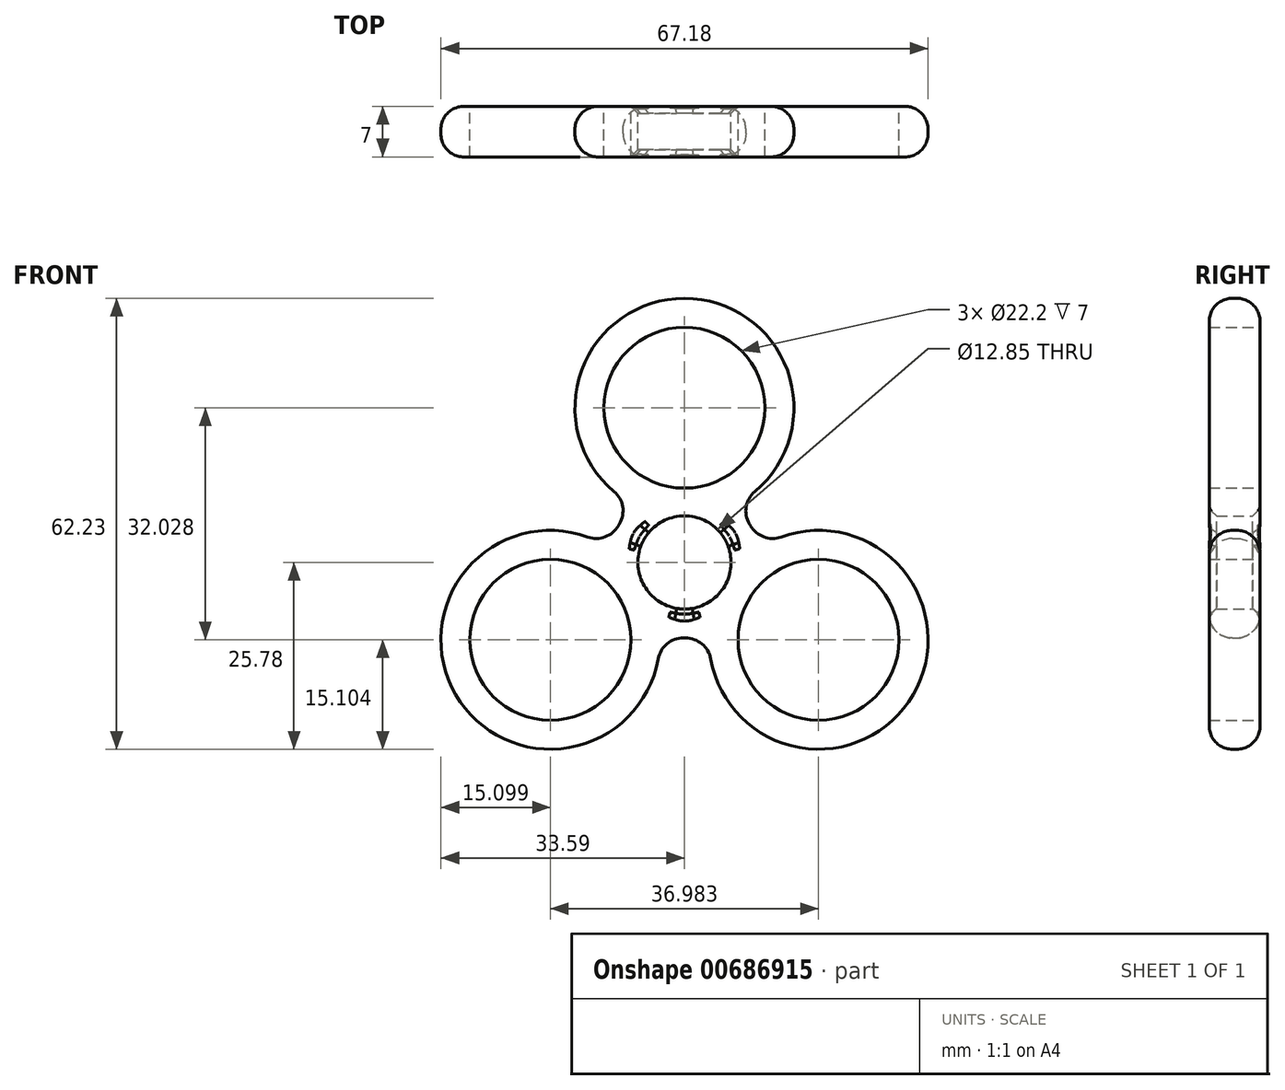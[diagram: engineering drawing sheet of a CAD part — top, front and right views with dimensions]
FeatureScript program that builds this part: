
annotation { "Feature Type Name" : "Feature", "Feature Type Description" : "" }
export const myFeature = defineFeature(function(context is Context, id is Id, definition is map)
    precondition{}
    {
        {
            var Q0;
            Q0=qCreatedBy(makeId("Front.planeOp"),FACE);
            var sketch = newSketch(context, id + "F0", { "sketchPlane" : qUnion([Q0])});
            skCircle(sketch, "E0", {"center": v(0, 0) * mm, "radius": 6.42 * mm});
            skLineSegment(sketch, "E1", {"start": v(0, 0) * mm, "end": v(0, 21.35) * mm, "construction": true});
            skLineSegment(sketch, "E2", {"start": v(0, 0) * mm, "end": v(18.5, -10.68) * mm, "construction": true});
            skLineSegment(sketch, "E3", {"start": v(0, 0) * mm, "end": v(-18.5, -10.68) * mm, "construction": true});
            skCircle(sketch, "E4", {"center": v(0, 21.35) * mm, "radius": 11.1 * mm});
            skCircle(sketch, "E5", {"center": v(18.5, -10.68) * mm, "radius": 11.1 * mm});
            skCircle(sketch, "E6", {"center": v(-18.5, -10.68) * mm, "radius": 11.1 * mm});
            skArc(sketch, "E7.0", {"start": v(9.72, 9.8) * mm, "mid": v(0, 36.45) * mm, "end": v(-9.72, 9.8) * mm});
            skArc(sketch, "E8.0", {"start": v(3.63, -13.32) * mm, "mid": v(31.57, -18.22) * mm, "end": v(13.34, 3.52) * mm});
            skArc(sketch, "E9.0", {"start": v(-13.34, 3.52) * mm, "mid": v(-31.57, -18.22) * mm, "end": v(-3.62, -13.32) * mm});
            skArc(sketch, "E10.0", {"start": v(9.1, 5.1) * mm, "mid": v(9.03, 5.21) * mm, "end": v(8.96, 5.33) * mm});
            skArc(sketch, "E11.trimOffspring", {"start": v(-0.12, -10.44) * mm, "mid": v(0, -10.44) * mm, "end": v(0.14, -10.44) * mm});
            skArc(sketch, "E12.trimOffspring", {"start": v(-8.96, 5.33) * mm, "mid": v(-9.03, 5.21) * mm, "end": v(-9.1, 5.1) * mm});
            skPoint(sketch, "E13.visualSharp", {"position": v(6.82, 7.88) * mm});
            skArc(sketch, "E13.filletArc", {"start": v(9.72, 9.8) * mm, "mid": v(8.52, 7.7) * mm, "end": v(8.96, 5.33) * mm});
            skPoint(sketch, "E14.visualSharp", {"position": v(10.24, 1.97) * mm});
            skArc(sketch, "E14.filletArc", {"start": v(9.1, 5.1) * mm, "mid": v(10.93, 3.53) * mm, "end": v(13.34, 3.52) * mm});
            skPoint(sketch, "E15.visualSharp", {"position": v(-6.82, 7.88) * mm});
            skArc(sketch, "E15.filletArc", {"start": v(-8.96, 5.33) * mm, "mid": v(-8.52, 7.7) * mm, "end": v(-9.72, 9.8) * mm});
            skPoint(sketch, "E16.visualSharp", {"position": v(-10.24, 1.97) * mm});
            skArc(sketch, "E16.filletArc", {"start": v(-13.34, 3.52) * mm, "mid": v(-10.93, 3.53) * mm, "end": v(-9.1, 5.1) * mm});
            skPoint(sketch, "E17.visualSharp", {"position": v(-3.41, -9.85) * mm});
            skArc(sketch, "E17.filletArc", {"start": v(-0.12, -10.44) * mm, "mid": v(-2.4, -11.23) * mm, "end": v(-3.62, -13.32) * mm});
            skPoint(sketch, "E18.visualSharp", {"position": v(3.41, -9.88) * mm});
            skArc(sketch, "E18.filletArc", {"start": v(3.63, -13.32) * mm, "mid": v(2.41, -11.24) * mm, "end": v(0.14, -10.44) * mm});
            skSolve(sketch);
        }
        {
            var Q0;
            Q0 = qSketchRegion(id + "F0", true);
            extrude(context, id + "F1", {"entities" : qUnion([Q0]), "endBound" : BoundingType.SYMMETRIC, "depth" : 7 * mm, "offsetDistance" : 25 * mm});
        }
        {
            var Q0;
            Q0=makeQuery(id+"F1.opExtrude","CAP_EDGE",EDGE,{"disambiguationData":[OSD([sQuery(id+"F0.wireOp",EDGE,"E15.filletArc")])],"isStart":false});
            var Q1;
            Q1=makeQuery(id+"F1.opExtrude","CAP_EDGE",EDGE,{"disambiguationData":[OSD([sQuery(id+"F0.wireOp",EDGE,"E15.filletArc")])],"isStart":true});
            fillet(context, id + "F2", {"entities" : qUnion([Q0, Q1]), "radius" : 3.2 * mm, "tangentPropagation" : true, "allowEdgeOverflow" : false});
        }
        {
            var Q0;
            Q0=makeQuery(id+"F1.opExtrude","CAP_EDGE",EDGE,{"disambiguationData":[OSD([sQuery(id+"F0.wireOp",EDGE,"E0")])],"isStart":false});
            var Q1;
            Q1=makeQuery(id+"F1.opExtrude","CAP_EDGE",EDGE,{"disambiguationData":[OSD([sQuery(id+"F0.wireOp",EDGE,"E0")])],"isStart":true});
            chamfer(context, id + "F3", {"entities" : qUnion([Q0, Q1]), "width" : 1 * mm, "tangentPropagation" : true});
        }
        {
            var Q0;
            {var subQ0=sQuery(id+"F0.wireOp",EDGE,"E15.filletArc");Q0=makeQuery(id+"F3.opChamfer","BLEND_EDGE",EDGE,{"blendedFrom":[makeQuery(id+"F1.opExtrude","CAP_EDGE",EDGE,{"disambiguationData":[OSD([sQuery(id+"F0.wireOp",EDGE,"E0")])],"isStart":true}),makeQuery(id+"F2.opFillet","BLEND_FACE",FACE,{"disambiguationData":[OSD([subQ0]),TDD([makeQuery(id+"F1.opExtrude","CAP_EDGE",EDGE,{"disambiguationData":[OSD([subQ0])],"isStart":true})])]})],"blendedInto":[makeQuery(id+"F2.opFillet","BLEND_FACE",FACE,{"disambiguationData":[OSD([subQ0]),TDD([makeQuery(id+"F1.opExtrude","CAP_EDGE",EDGE,{"disambiguationData":[OSD([subQ0])],"isStart":true})])]})]});}
            var Q1;
            {var subQ0=sQuery(id+"F0.wireOp",EDGE,"E16.filletArc");Q1=makeQuery(id+"F3.opChamfer","BLEND_EDGE",EDGE,{"blendedFrom":[makeQuery(id+"F1.opExtrude","CAP_EDGE",EDGE,{"disambiguationData":[OSD([sQuery(id+"F0.wireOp",EDGE,"E0")])],"isStart":true}),makeQuery(id+"F2.opFillet","BLEND_FACE",FACE,{"disambiguationData":[OSD([subQ0]),TDD([makeQuery(id+"F1.opExtrude","CAP_EDGE",EDGE,{"disambiguationData":[OSD([subQ0])],"isStart":true})])]})],"blendedInto":[makeQuery(id+"F2.opFillet","BLEND_FACE",FACE,{"disambiguationData":[OSD([subQ0]),TDD([makeQuery(id+"F1.opExtrude","CAP_EDGE",EDGE,{"disambiguationData":[OSD([subQ0])],"isStart":true})])]})]});}
            var Q2;
            {var subQ0=sQuery(id+"F0.wireOp",EDGE,"E12.trimOffspring");Q2=makeQuery(id+"F3.opChamfer","BLEND_EDGE",EDGE,{"blendedFrom":[makeQuery(id+"F1.opExtrude","CAP_EDGE",EDGE,{"disambiguationData":[OSD([sQuery(id+"F0.wireOp",EDGE,"E0")])],"isStart":true}),makeQuery(id+"F2.opFillet","BLEND_FACE",FACE,{"disambiguationData":[OSD([subQ0]),TDD([makeQuery(id+"F1.opExtrude","CAP_EDGE",EDGE,{"disambiguationData":[OSD([subQ0])],"isStart":true})])]})],"blendedInto":[makeQuery(id+"F2.opFillet","BLEND_FACE",FACE,{"disambiguationData":[OSD([subQ0]),TDD([makeQuery(id+"F1.opExtrude","CAP_EDGE",EDGE,{"disambiguationData":[OSD([subQ0])],"isStart":true})])]})]});}
            var Q3;
            {var subQ0=sQuery(id+"F0.wireOp",EDGE,"E0");Q3=makeQuery(id+"F3.opChamfer","BLEND_EDGE",EDGE,{"disambiguationData":[OD(2.0)],"blendedFrom":[makeQuery(id+"F1.opExtrude","CAP_EDGE",EDGE,{"disambiguationData":[OSD([subQ0])],"isStart":true}),makeQuery(id+"F1.opExtrude","CAP_FACE",FACE,{"disambiguationData":[OSD([subQ0,sQuery(id+"F0.wireOp",EDGE,"E4"),sQuery(id+"F0.wireOp",EDGE,"E5"),sQuery(id+"F0.wireOp",EDGE,"E6"),sQuery(id+"F0.wireOp",EDGE,"E7.0"),sQuery(id+"F0.wireOp",EDGE,"E8.0"),sQuery(id+"F0.wireOp",EDGE,"E9.0"),sQuery(id+"F0.wireOp",EDGE,"E10.0"),sQuery(id+"F0.wireOp",EDGE,"E11.trimOffspring"),sQuery(id+"F0.wireOp",EDGE,"E12.trimOffspring"),sQuery(id+"F0.wireOp",EDGE,"E13.filletArc"),sQuery(id+"F0.wireOp",EDGE,"E14.filletArc"),sQuery(id+"F0.wireOp",EDGE,"E15.filletArc"),sQuery(id+"F0.wireOp",EDGE,"E16.filletArc"),sQuery(id+"F0.wireOp",EDGE,"E17.filletArc"),sQuery(id+"F0.wireOp",EDGE,"E18.filletArc")])],"isStart":true})],"blendedInto":[makeQuery(id+"F1.opExtrude","CAP_FACE",FACE,{"disambiguationData":[OSD([subQ0,sQuery(id+"F0.wireOp",EDGE,"E4"),sQuery(id+"F0.wireOp",EDGE,"E5"),sQuery(id+"F0.wireOp",EDGE,"E6"),sQuery(id+"F0.wireOp",EDGE,"E7.0"),sQuery(id+"F0.wireOp",EDGE,"E8.0"),sQuery(id+"F0.wireOp",EDGE,"E9.0"),sQuery(id+"F0.wireOp",EDGE,"E10.0"),sQuery(id+"F0.wireOp",EDGE,"E11.trimOffspring"),sQuery(id+"F0.wireOp",EDGE,"E12.trimOffspring"),sQuery(id+"F0.wireOp",EDGE,"E13.filletArc"),sQuery(id+"F0.wireOp",EDGE,"E14.filletArc"),sQuery(id+"F0.wireOp",EDGE,"E15.filletArc"),sQuery(id+"F0.wireOp",EDGE,"E16.filletArc"),sQuery(id+"F0.wireOp",EDGE,"E17.filletArc"),sQuery(id+"F0.wireOp",EDGE,"E18.filletArc")])],"isStart":true})]});}
            var Q4;
            {var subQ0=sQuery(id+"F0.wireOp",EDGE,"E0");Q4=makeQuery(id+"F3.opChamfer","BLEND_EDGE",EDGE,{"disambiguationData":[OD(0.0)],"blendedFrom":[makeQuery(id+"F1.opExtrude","CAP_EDGE",EDGE,{"disambiguationData":[OSD([subQ0])],"isStart":true}),makeQuery(id+"F1.opExtrude","CAP_FACE",FACE,{"disambiguationData":[OSD([subQ0,sQuery(id+"F0.wireOp",EDGE,"E4"),sQuery(id+"F0.wireOp",EDGE,"E5"),sQuery(id+"F0.wireOp",EDGE,"E6"),sQuery(id+"F0.wireOp",EDGE,"E7.0"),sQuery(id+"F0.wireOp",EDGE,"E8.0"),sQuery(id+"F0.wireOp",EDGE,"E9.0"),sQuery(id+"F0.wireOp",EDGE,"E10.0"),sQuery(id+"F0.wireOp",EDGE,"E11.trimOffspring"),sQuery(id+"F0.wireOp",EDGE,"E12.trimOffspring"),sQuery(id+"F0.wireOp",EDGE,"E13.filletArc"),sQuery(id+"F0.wireOp",EDGE,"E14.filletArc"),sQuery(id+"F0.wireOp",EDGE,"E15.filletArc"),sQuery(id+"F0.wireOp",EDGE,"E16.filletArc"),sQuery(id+"F0.wireOp",EDGE,"E17.filletArc"),sQuery(id+"F0.wireOp",EDGE,"E18.filletArc")])],"isStart":true})],"blendedInto":[makeQuery(id+"F1.opExtrude","CAP_FACE",FACE,{"disambiguationData":[OSD([subQ0,sQuery(id+"F0.wireOp",EDGE,"E4"),sQuery(id+"F0.wireOp",EDGE,"E5"),sQuery(id+"F0.wireOp",EDGE,"E6"),sQuery(id+"F0.wireOp",EDGE,"E7.0"),sQuery(id+"F0.wireOp",EDGE,"E8.0"),sQuery(id+"F0.wireOp",EDGE,"E9.0"),sQuery(id+"F0.wireOp",EDGE,"E10.0"),sQuery(id+"F0.wireOp",EDGE,"E11.trimOffspring"),sQuery(id+"F0.wireOp",EDGE,"E12.trimOffspring"),sQuery(id+"F0.wireOp",EDGE,"E13.filletArc"),sQuery(id+"F0.wireOp",EDGE,"E14.filletArc"),sQuery(id+"F0.wireOp",EDGE,"E15.filletArc"),sQuery(id+"F0.wireOp",EDGE,"E16.filletArc"),sQuery(id+"F0.wireOp",EDGE,"E17.filletArc"),sQuery(id+"F0.wireOp",EDGE,"E18.filletArc")])],"isStart":true})]});}
            var Q5;
            {var subQ0=sQuery(id+"F0.wireOp",EDGE,"E13.filletArc");Q5=makeQuery(id+"F3.opChamfer","BLEND_EDGE",EDGE,{"blendedFrom":[makeQuery(id+"F1.opExtrude","CAP_EDGE",EDGE,{"disambiguationData":[OSD([sQuery(id+"F0.wireOp",EDGE,"E0")])],"isStart":true}),makeQuery(id+"F2.opFillet","BLEND_FACE",FACE,{"disambiguationData":[OSD([subQ0]),TDD([makeQuery(id+"F1.opExtrude","CAP_EDGE",EDGE,{"disambiguationData":[OSD([subQ0])],"isStart":true})])]})],"blendedInto":[makeQuery(id+"F2.opFillet","BLEND_FACE",FACE,{"disambiguationData":[OSD([subQ0]),TDD([makeQuery(id+"F1.opExtrude","CAP_EDGE",EDGE,{"disambiguationData":[OSD([subQ0])],"isStart":true})])]})]});}
            var Q6;
            {var subQ0=sQuery(id+"F0.wireOp",EDGE,"E14.filletArc");Q6=makeQuery(id+"F3.opChamfer","BLEND_EDGE",EDGE,{"blendedFrom":[makeQuery(id+"F1.opExtrude","CAP_EDGE",EDGE,{"disambiguationData":[OSD([sQuery(id+"F0.wireOp",EDGE,"E0")])],"isStart":true}),makeQuery(id+"F2.opFillet","BLEND_FACE",FACE,{"disambiguationData":[OSD([subQ0]),TDD([makeQuery(id+"F1.opExtrude","CAP_EDGE",EDGE,{"disambiguationData":[OSD([subQ0])],"isStart":true})])]})],"blendedInto":[makeQuery(id+"F2.opFillet","BLEND_FACE",FACE,{"disambiguationData":[OSD([subQ0]),TDD([makeQuery(id+"F1.opExtrude","CAP_EDGE",EDGE,{"disambiguationData":[OSD([subQ0])],"isStart":true})])]})]});}
            var Q7;
            {var subQ0=sQuery(id+"F0.wireOp",EDGE,"E10.0");Q7=makeQuery(id+"F3.opChamfer","BLEND_EDGE",EDGE,{"blendedFrom":[makeQuery(id+"F1.opExtrude","CAP_EDGE",EDGE,{"disambiguationData":[OSD([sQuery(id+"F0.wireOp",EDGE,"E0")])],"isStart":true}),makeQuery(id+"F2.opFillet","BLEND_FACE",FACE,{"disambiguationData":[OSD([subQ0]),TDD([makeQuery(id+"F1.opExtrude","CAP_EDGE",EDGE,{"disambiguationData":[OSD([subQ0])],"isStart":true})])]})],"blendedInto":[makeQuery(id+"F2.opFillet","BLEND_FACE",FACE,{"disambiguationData":[OSD([subQ0]),TDD([makeQuery(id+"F1.opExtrude","CAP_EDGE",EDGE,{"disambiguationData":[OSD([subQ0])],"isStart":true})])]})]});}
            var Q8;
            {var subQ0=sQuery(id+"F0.wireOp",EDGE,"E0");Q8=makeQuery(id+"F3.opChamfer","BLEND_EDGE",EDGE,{"disambiguationData":[OD(1.0)],"blendedFrom":[makeQuery(id+"F1.opExtrude","CAP_EDGE",EDGE,{"disambiguationData":[OSD([subQ0])],"isStart":true}),makeQuery(id+"F1.opExtrude","CAP_FACE",FACE,{"disambiguationData":[OSD([subQ0,sQuery(id+"F0.wireOp",EDGE,"E4"),sQuery(id+"F0.wireOp",EDGE,"E5"),sQuery(id+"F0.wireOp",EDGE,"E6"),sQuery(id+"F0.wireOp",EDGE,"E7.0"),sQuery(id+"F0.wireOp",EDGE,"E8.0"),sQuery(id+"F0.wireOp",EDGE,"E9.0"),sQuery(id+"F0.wireOp",EDGE,"E10.0"),sQuery(id+"F0.wireOp",EDGE,"E11.trimOffspring"),sQuery(id+"F0.wireOp",EDGE,"E12.trimOffspring"),sQuery(id+"F0.wireOp",EDGE,"E13.filletArc"),sQuery(id+"F0.wireOp",EDGE,"E14.filletArc"),sQuery(id+"F0.wireOp",EDGE,"E15.filletArc"),sQuery(id+"F0.wireOp",EDGE,"E16.filletArc"),sQuery(id+"F0.wireOp",EDGE,"E17.filletArc"),sQuery(id+"F0.wireOp",EDGE,"E18.filletArc")])],"isStart":true})],"blendedInto":[makeQuery(id+"F1.opExtrude","CAP_FACE",FACE,{"disambiguationData":[OSD([subQ0,sQuery(id+"F0.wireOp",EDGE,"E4"),sQuery(id+"F0.wireOp",EDGE,"E5"),sQuery(id+"F0.wireOp",EDGE,"E6"),sQuery(id+"F0.wireOp",EDGE,"E7.0"),sQuery(id+"F0.wireOp",EDGE,"E8.0"),sQuery(id+"F0.wireOp",EDGE,"E9.0"),sQuery(id+"F0.wireOp",EDGE,"E10.0"),sQuery(id+"F0.wireOp",EDGE,"E11.trimOffspring"),sQuery(id+"F0.wireOp",EDGE,"E12.trimOffspring"),sQuery(id+"F0.wireOp",EDGE,"E13.filletArc"),sQuery(id+"F0.wireOp",EDGE,"E14.filletArc"),sQuery(id+"F0.wireOp",EDGE,"E15.filletArc"),sQuery(id+"F0.wireOp",EDGE,"E16.filletArc"),sQuery(id+"F0.wireOp",EDGE,"E17.filletArc"),sQuery(id+"F0.wireOp",EDGE,"E18.filletArc")])],"isStart":true})]});}
            var Q9;
            {var subQ0=sQuery(id+"F0.wireOp",EDGE,"E18.filletArc");Q9=makeQuery(id+"F3.opChamfer","BLEND_EDGE",EDGE,{"blendedFrom":[makeQuery(id+"F1.opExtrude","CAP_EDGE",EDGE,{"disambiguationData":[OSD([sQuery(id+"F0.wireOp",EDGE,"E0")])],"isStart":true}),makeQuery(id+"F2.opFillet","BLEND_FACE",FACE,{"disambiguationData":[OSD([subQ0]),TDD([makeQuery(id+"F1.opExtrude","CAP_EDGE",EDGE,{"disambiguationData":[OSD([subQ0])],"isStart":true})])]})],"blendedInto":[makeQuery(id+"F2.opFillet","BLEND_FACE",FACE,{"disambiguationData":[OSD([subQ0]),TDD([makeQuery(id+"F1.opExtrude","CAP_EDGE",EDGE,{"disambiguationData":[OSD([subQ0])],"isStart":true})])]})]});}
            var Q10;
            {var subQ0=sQuery(id+"F0.wireOp",EDGE,"E17.filletArc");Q10=makeQuery(id+"F3.opChamfer","BLEND_EDGE",EDGE,{"blendedFrom":[makeQuery(id+"F1.opExtrude","CAP_EDGE",EDGE,{"disambiguationData":[OSD([sQuery(id+"F0.wireOp",EDGE,"E0")])],"isStart":true}),makeQuery(id+"F2.opFillet","BLEND_FACE",FACE,{"disambiguationData":[OSD([subQ0]),TDD([makeQuery(id+"F1.opExtrude","CAP_EDGE",EDGE,{"disambiguationData":[OSD([subQ0])],"isStart":true})])]})],"blendedInto":[makeQuery(id+"F2.opFillet","BLEND_FACE",FACE,{"disambiguationData":[OSD([subQ0]),TDD([makeQuery(id+"F1.opExtrude","CAP_EDGE",EDGE,{"disambiguationData":[OSD([subQ0])],"isStart":true})])]})]});}
            var Q11;
            {var subQ0=sQuery(id+"F0.wireOp",EDGE,"E11.trimOffspring");Q11=makeQuery(id+"F3.opChamfer","BLEND_EDGE",EDGE,{"blendedFrom":[makeQuery(id+"F1.opExtrude","CAP_EDGE",EDGE,{"disambiguationData":[OSD([sQuery(id+"F0.wireOp",EDGE,"E0")])],"isStart":true}),makeQuery(id+"F2.opFillet","BLEND_FACE",FACE,{"disambiguationData":[OSD([subQ0]),TDD([makeQuery(id+"F1.opExtrude","CAP_EDGE",EDGE,{"disambiguationData":[OSD([subQ0])],"isStart":true})])]})],"blendedInto":[makeQuery(id+"F2.opFillet","BLEND_FACE",FACE,{"disambiguationData":[OSD([subQ0]),TDD([makeQuery(id+"F1.opExtrude","CAP_EDGE",EDGE,{"disambiguationData":[OSD([subQ0])],"isStart":true})])]})]});}
            var Q12;
            {var subQ0=sQuery(id+"F0.wireOp",EDGE,"E0");Q12=makeQuery(id+"F3.opChamfer","BLEND_EDGE",EDGE,{"disambiguationData":[OD(1.0)],"blendedFrom":[makeQuery(id+"F1.opExtrude","CAP_EDGE",EDGE,{"disambiguationData":[OSD([subQ0])],"isStart":false}),makeQuery(id+"F1.opExtrude","CAP_FACE",FACE,{"disambiguationData":[OSD([subQ0,sQuery(id+"F0.wireOp",EDGE,"E4"),sQuery(id+"F0.wireOp",EDGE,"E5"),sQuery(id+"F0.wireOp",EDGE,"E6"),sQuery(id+"F0.wireOp",EDGE,"E7.0"),sQuery(id+"F0.wireOp",EDGE,"E8.0"),sQuery(id+"F0.wireOp",EDGE,"E9.0"),sQuery(id+"F0.wireOp",EDGE,"E10.0"),sQuery(id+"F0.wireOp",EDGE,"E11.trimOffspring"),sQuery(id+"F0.wireOp",EDGE,"E12.trimOffspring"),sQuery(id+"F0.wireOp",EDGE,"E13.filletArc"),sQuery(id+"F0.wireOp",EDGE,"E14.filletArc"),sQuery(id+"F0.wireOp",EDGE,"E15.filletArc"),sQuery(id+"F0.wireOp",EDGE,"E16.filletArc"),sQuery(id+"F0.wireOp",EDGE,"E17.filletArc"),sQuery(id+"F0.wireOp",EDGE,"E18.filletArc")])],"isStart":false})],"blendedInto":[makeQuery(id+"F1.opExtrude","CAP_FACE",FACE,{"disambiguationData":[OSD([subQ0,sQuery(id+"F0.wireOp",EDGE,"E4"),sQuery(id+"F0.wireOp",EDGE,"E5"),sQuery(id+"F0.wireOp",EDGE,"E6"),sQuery(id+"F0.wireOp",EDGE,"E7.0"),sQuery(id+"F0.wireOp",EDGE,"E8.0"),sQuery(id+"F0.wireOp",EDGE,"E9.0"),sQuery(id+"F0.wireOp",EDGE,"E10.0"),sQuery(id+"F0.wireOp",EDGE,"E11.trimOffspring"),sQuery(id+"F0.wireOp",EDGE,"E12.trimOffspring"),sQuery(id+"F0.wireOp",EDGE,"E13.filletArc"),sQuery(id+"F0.wireOp",EDGE,"E14.filletArc"),sQuery(id+"F0.wireOp",EDGE,"E15.filletArc"),sQuery(id+"F0.wireOp",EDGE,"E16.filletArc"),sQuery(id+"F0.wireOp",EDGE,"E17.filletArc"),sQuery(id+"F0.wireOp",EDGE,"E18.filletArc")])],"isStart":false})]});}
            var Q13;
            {var subQ0=sQuery(id+"F0.wireOp",EDGE,"E14.filletArc");Q13=makeQuery(id+"F3.opChamfer","BLEND_EDGE",EDGE,{"blendedFrom":[makeQuery(id+"F1.opExtrude","CAP_EDGE",EDGE,{"disambiguationData":[OSD([sQuery(id+"F0.wireOp",EDGE,"E0")])],"isStart":false}),makeQuery(id+"F2.opFillet","BLEND_FACE",FACE,{"disambiguationData":[OSD([subQ0]),TDD([makeQuery(id+"F1.opExtrude","CAP_EDGE",EDGE,{"disambiguationData":[OSD([subQ0])],"isStart":false})])]})],"blendedInto":[makeQuery(id+"F2.opFillet","BLEND_FACE",FACE,{"disambiguationData":[OSD([subQ0]),TDD([makeQuery(id+"F1.opExtrude","CAP_EDGE",EDGE,{"disambiguationData":[OSD([subQ0])],"isStart":false})])]})]});}
            var Q14;
            {var subQ0=sQuery(id+"F0.wireOp",EDGE,"E10.0");Q14=makeQuery(id+"F3.opChamfer","BLEND_EDGE",EDGE,{"blendedFrom":[makeQuery(id+"F1.opExtrude","CAP_EDGE",EDGE,{"disambiguationData":[OSD([sQuery(id+"F0.wireOp",EDGE,"E0")])],"isStart":false}),makeQuery(id+"F2.opFillet","BLEND_FACE",FACE,{"disambiguationData":[OSD([subQ0]),TDD([makeQuery(id+"F1.opExtrude","CAP_EDGE",EDGE,{"disambiguationData":[OSD([subQ0])],"isStart":false})])]})],"blendedInto":[makeQuery(id+"F2.opFillet","BLEND_FACE",FACE,{"disambiguationData":[OSD([subQ0]),TDD([makeQuery(id+"F1.opExtrude","CAP_EDGE",EDGE,{"disambiguationData":[OSD([subQ0])],"isStart":false})])]})]});}
            var Q15;
            {var subQ0=sQuery(id+"F0.wireOp",EDGE,"E13.filletArc");Q15=makeQuery(id+"F3.opChamfer","BLEND_EDGE",EDGE,{"blendedFrom":[makeQuery(id+"F1.opExtrude","CAP_EDGE",EDGE,{"disambiguationData":[OSD([sQuery(id+"F0.wireOp",EDGE,"E0")])],"isStart":false}),makeQuery(id+"F2.opFillet","BLEND_FACE",FACE,{"disambiguationData":[OSD([subQ0]),TDD([makeQuery(id+"F1.opExtrude","CAP_EDGE",EDGE,{"disambiguationData":[OSD([subQ0])],"isStart":false})])]})],"blendedInto":[makeQuery(id+"F2.opFillet","BLEND_FACE",FACE,{"disambiguationData":[OSD([subQ0]),TDD([makeQuery(id+"F1.opExtrude","CAP_EDGE",EDGE,{"disambiguationData":[OSD([subQ0])],"isStart":false})])]})]});}
            var Q16;
            {var subQ0=sQuery(id+"F0.wireOp",EDGE,"E0");Q16=makeQuery(id+"F3.opChamfer","BLEND_EDGE",EDGE,{"disambiguationData":[OD(0.0)],"blendedFrom":[makeQuery(id+"F1.opExtrude","CAP_EDGE",EDGE,{"disambiguationData":[OSD([subQ0])],"isStart":false}),makeQuery(id+"F1.opExtrude","CAP_FACE",FACE,{"disambiguationData":[OSD([subQ0,sQuery(id+"F0.wireOp",EDGE,"E4"),sQuery(id+"F0.wireOp",EDGE,"E5"),sQuery(id+"F0.wireOp",EDGE,"E6"),sQuery(id+"F0.wireOp",EDGE,"E7.0"),sQuery(id+"F0.wireOp",EDGE,"E8.0"),sQuery(id+"F0.wireOp",EDGE,"E9.0"),sQuery(id+"F0.wireOp",EDGE,"E10.0"),sQuery(id+"F0.wireOp",EDGE,"E11.trimOffspring"),sQuery(id+"F0.wireOp",EDGE,"E12.trimOffspring"),sQuery(id+"F0.wireOp",EDGE,"E13.filletArc"),sQuery(id+"F0.wireOp",EDGE,"E14.filletArc"),sQuery(id+"F0.wireOp",EDGE,"E15.filletArc"),sQuery(id+"F0.wireOp",EDGE,"E16.filletArc"),sQuery(id+"F0.wireOp",EDGE,"E17.filletArc"),sQuery(id+"F0.wireOp",EDGE,"E18.filletArc")])],"isStart":false})],"blendedInto":[makeQuery(id+"F1.opExtrude","CAP_FACE",FACE,{"disambiguationData":[OSD([subQ0,sQuery(id+"F0.wireOp",EDGE,"E4"),sQuery(id+"F0.wireOp",EDGE,"E5"),sQuery(id+"F0.wireOp",EDGE,"E6"),sQuery(id+"F0.wireOp",EDGE,"E7.0"),sQuery(id+"F0.wireOp",EDGE,"E8.0"),sQuery(id+"F0.wireOp",EDGE,"E9.0"),sQuery(id+"F0.wireOp",EDGE,"E10.0"),sQuery(id+"F0.wireOp",EDGE,"E11.trimOffspring"),sQuery(id+"F0.wireOp",EDGE,"E12.trimOffspring"),sQuery(id+"F0.wireOp",EDGE,"E13.filletArc"),sQuery(id+"F0.wireOp",EDGE,"E14.filletArc"),sQuery(id+"F0.wireOp",EDGE,"E15.filletArc"),sQuery(id+"F0.wireOp",EDGE,"E16.filletArc"),sQuery(id+"F0.wireOp",EDGE,"E17.filletArc"),sQuery(id+"F0.wireOp",EDGE,"E18.filletArc")])],"isStart":false})]});}
            var Q17;
            {var subQ0=sQuery(id+"F0.wireOp",EDGE,"E15.filletArc");Q17=makeQuery(id+"F3.opChamfer","BLEND_EDGE",EDGE,{"blendedFrom":[makeQuery(id+"F1.opExtrude","CAP_EDGE",EDGE,{"disambiguationData":[OSD([sQuery(id+"F0.wireOp",EDGE,"E0")])],"isStart":false}),makeQuery(id+"F2.opFillet","BLEND_FACE",FACE,{"disambiguationData":[OSD([subQ0]),TDD([makeQuery(id+"F1.opExtrude","CAP_EDGE",EDGE,{"disambiguationData":[OSD([subQ0])],"isStart":false})])]})],"blendedInto":[makeQuery(id+"F2.opFillet","BLEND_FACE",FACE,{"disambiguationData":[OSD([subQ0]),TDD([makeQuery(id+"F1.opExtrude","CAP_EDGE",EDGE,{"disambiguationData":[OSD([subQ0])],"isStart":false})])]})]});}
            var Q18;
            {var subQ0=sQuery(id+"F0.wireOp",EDGE,"E12.trimOffspring");Q18=makeQuery(id+"F3.opChamfer","BLEND_EDGE",EDGE,{"blendedFrom":[makeQuery(id+"F1.opExtrude","CAP_EDGE",EDGE,{"disambiguationData":[OSD([sQuery(id+"F0.wireOp",EDGE,"E0")])],"isStart":false}),makeQuery(id+"F2.opFillet","BLEND_FACE",FACE,{"disambiguationData":[OSD([subQ0]),TDD([makeQuery(id+"F1.opExtrude","CAP_EDGE",EDGE,{"disambiguationData":[OSD([subQ0])],"isStart":false})])]})],"blendedInto":[makeQuery(id+"F2.opFillet","BLEND_FACE",FACE,{"disambiguationData":[OSD([subQ0]),TDD([makeQuery(id+"F1.opExtrude","CAP_EDGE",EDGE,{"disambiguationData":[OSD([subQ0])],"isStart":false})])]})]});}
            var Q19;
            {var subQ0=sQuery(id+"F0.wireOp",EDGE,"E16.filletArc");Q19=makeQuery(id+"F3.opChamfer","BLEND_EDGE",EDGE,{"blendedFrom":[makeQuery(id+"F1.opExtrude","CAP_EDGE",EDGE,{"disambiguationData":[OSD([sQuery(id+"F0.wireOp",EDGE,"E0")])],"isStart":false}),makeQuery(id+"F2.opFillet","BLEND_FACE",FACE,{"disambiguationData":[OSD([subQ0]),TDD([makeQuery(id+"F1.opExtrude","CAP_EDGE",EDGE,{"disambiguationData":[OSD([subQ0])],"isStart":false})])]})],"blendedInto":[makeQuery(id+"F2.opFillet","BLEND_FACE",FACE,{"disambiguationData":[OSD([subQ0]),TDD([makeQuery(id+"F1.opExtrude","CAP_EDGE",EDGE,{"disambiguationData":[OSD([subQ0])],"isStart":false})])]})]});}
            var Q20;
            {var subQ0=sQuery(id+"F0.wireOp",EDGE,"E0");Q20=makeQuery(id+"F3.opChamfer","BLEND_EDGE",EDGE,{"disambiguationData":[OD(2.0)],"blendedFrom":[makeQuery(id+"F1.opExtrude","CAP_EDGE",EDGE,{"disambiguationData":[OSD([subQ0])],"isStart":false}),makeQuery(id+"F1.opExtrude","CAP_FACE",FACE,{"disambiguationData":[OSD([subQ0,sQuery(id+"F0.wireOp",EDGE,"E4"),sQuery(id+"F0.wireOp",EDGE,"E5"),sQuery(id+"F0.wireOp",EDGE,"E6"),sQuery(id+"F0.wireOp",EDGE,"E7.0"),sQuery(id+"F0.wireOp",EDGE,"E8.0"),sQuery(id+"F0.wireOp",EDGE,"E9.0"),sQuery(id+"F0.wireOp",EDGE,"E10.0"),sQuery(id+"F0.wireOp",EDGE,"E11.trimOffspring"),sQuery(id+"F0.wireOp",EDGE,"E12.trimOffspring"),sQuery(id+"F0.wireOp",EDGE,"E13.filletArc"),sQuery(id+"F0.wireOp",EDGE,"E14.filletArc"),sQuery(id+"F0.wireOp",EDGE,"E15.filletArc"),sQuery(id+"F0.wireOp",EDGE,"E16.filletArc"),sQuery(id+"F0.wireOp",EDGE,"E17.filletArc"),sQuery(id+"F0.wireOp",EDGE,"E18.filletArc")])],"isStart":false})],"blendedInto":[makeQuery(id+"F1.opExtrude","CAP_FACE",FACE,{"disambiguationData":[OSD([subQ0,sQuery(id+"F0.wireOp",EDGE,"E4"),sQuery(id+"F0.wireOp",EDGE,"E5"),sQuery(id+"F0.wireOp",EDGE,"E6"),sQuery(id+"F0.wireOp",EDGE,"E7.0"),sQuery(id+"F0.wireOp",EDGE,"E8.0"),sQuery(id+"F0.wireOp",EDGE,"E9.0"),sQuery(id+"F0.wireOp",EDGE,"E10.0"),sQuery(id+"F0.wireOp",EDGE,"E11.trimOffspring"),sQuery(id+"F0.wireOp",EDGE,"E12.trimOffspring"),sQuery(id+"F0.wireOp",EDGE,"E13.filletArc"),sQuery(id+"F0.wireOp",EDGE,"E14.filletArc"),sQuery(id+"F0.wireOp",EDGE,"E15.filletArc"),sQuery(id+"F0.wireOp",EDGE,"E16.filletArc"),sQuery(id+"F0.wireOp",EDGE,"E17.filletArc"),sQuery(id+"F0.wireOp",EDGE,"E18.filletArc")])],"isStart":false})]});}
            var Q21;
            {var subQ0=sQuery(id+"F0.wireOp",EDGE,"E17.filletArc");Q21=makeQuery(id+"F3.opChamfer","BLEND_EDGE",EDGE,{"blendedFrom":[makeQuery(id+"F1.opExtrude","CAP_EDGE",EDGE,{"disambiguationData":[OSD([sQuery(id+"F0.wireOp",EDGE,"E0")])],"isStart":false}),makeQuery(id+"F2.opFillet","BLEND_FACE",FACE,{"disambiguationData":[OSD([subQ0]),TDD([makeQuery(id+"F1.opExtrude","CAP_EDGE",EDGE,{"disambiguationData":[OSD([subQ0])],"isStart":false})])]})],"blendedInto":[makeQuery(id+"F2.opFillet","BLEND_FACE",FACE,{"disambiguationData":[OSD([subQ0]),TDD([makeQuery(id+"F1.opExtrude","CAP_EDGE",EDGE,{"disambiguationData":[OSD([subQ0])],"isStart":false})])]})]});}
            var Q22;
            {var subQ0=sQuery(id+"F0.wireOp",EDGE,"E11.trimOffspring");Q22=makeQuery(id+"F3.opChamfer","BLEND_EDGE",EDGE,{"blendedFrom":[makeQuery(id+"F1.opExtrude","CAP_EDGE",EDGE,{"disambiguationData":[OSD([sQuery(id+"F0.wireOp",EDGE,"E0")])],"isStart":false}),makeQuery(id+"F2.opFillet","BLEND_FACE",FACE,{"disambiguationData":[OSD([subQ0]),TDD([makeQuery(id+"F1.opExtrude","CAP_EDGE",EDGE,{"disambiguationData":[OSD([subQ0])],"isStart":false})])]})],"blendedInto":[makeQuery(id+"F2.opFillet","BLEND_FACE",FACE,{"disambiguationData":[OSD([subQ0]),TDD([makeQuery(id+"F1.opExtrude","CAP_EDGE",EDGE,{"disambiguationData":[OSD([subQ0])],"isStart":false})])]})]});}
            var Q23;
            {var subQ0=sQuery(id+"F0.wireOp",EDGE,"E18.filletArc");Q23=makeQuery(id+"F3.opChamfer","BLEND_EDGE",EDGE,{"blendedFrom":[makeQuery(id+"F1.opExtrude","CAP_EDGE",EDGE,{"disambiguationData":[OSD([sQuery(id+"F0.wireOp",EDGE,"E0")])],"isStart":false}),makeQuery(id+"F2.opFillet","BLEND_FACE",FACE,{"disambiguationData":[OSD([subQ0]),TDD([makeQuery(id+"F1.opExtrude","CAP_EDGE",EDGE,{"disambiguationData":[OSD([subQ0])],"isStart":false})])]})],"blendedInto":[makeQuery(id+"F2.opFillet","BLEND_FACE",FACE,{"disambiguationData":[OSD([subQ0]),TDD([makeQuery(id+"F1.opExtrude","CAP_EDGE",EDGE,{"disambiguationData":[OSD([subQ0])],"isStart":false})])]})]});}
            fillet(context, id + "F4", {"entities" : qUnion([Q0, Q1, Q2, Q3, Q4, Q5, Q6, Q7, Q8, Q9, Q10, Q11, Q12, Q13, Q14, Q15, Q16, Q17, Q18, Q19, Q20, Q21, Q22, Q23]), "radius" : 1 * mm, "tangentPropagation" : true, "allowEdgeOverflow" : false});
        }
    });
